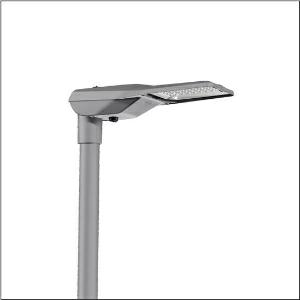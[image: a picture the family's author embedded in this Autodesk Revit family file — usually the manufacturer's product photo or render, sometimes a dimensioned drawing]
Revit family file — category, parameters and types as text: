
# Revit family: streetlight_sl_21_iq_mini___st1_0a_5xe2d31y08hb_7569
name_source: partatom
category: Lighting Fixtures
units: mm (PartAtom-declared; Revit-internal decimal feet)

## family parameters
Cut with Voids When Loaded = No
Host = Face
Light Source = No
Part Type = Normal
Room Calculation Point = No
Round Connector Dimension = Use Diameter
Shared = No

## types (1)
- --- (1 x LED, 9750 lm, 71 W, 3000K)
    Apparent Load = 71 VA
    CIE Flux Codes = 37 72 97 100 100
    Color Rendering = 70
    Color Temperature = 3000K
    Default Elevation = 1800 mm
    Description = Streetlight SL 21 iQ mini, mast luminaire, primary light control with lens, of PMMA, primary optical cover: cover, of toughened safety glass, transparent, light distribution: ST1.0a, light emission: direct distribution, primary light characteristic: asymmetric, installation type: post-top, side-entry, LED, High Power LED, rated luminous flux: 9.750lm, luminous efficacy: 137lm/W, light colour: 730, colour temperature: 3000K, control: presetting dimming logarithmic, Street-Remote, Auto-Match, Temp-Guard, Lumen-Switch, Night-Set, Smart-Wire, Light-Fading, Desk-Remote (wireless, voltage-free reading and setting of iQ features in the workshop via application-optimized NFC function/RFID function), optimised constant luminous flux control (CLO 2.0), mains connection: 220..240V, AC, 50/60Hz, start of lifetime: 71W, end of service life: 75W, reduction: 30W, luminaire housing, of diecast aluminium, powder-coated, Siteco® metallic grey (DB 702S), corrosivity category C5 mid according to DIN EN ISO 12944, please order mast flange separately, inclination adjustable: 0°, 5°, 10°, 15°, sealing non-destructively replaceable, multi-level sealing system, length: 628mm, width: 235mm, height: 110mm, mast flange for spigot size: 42mm (side-entry): 5XC10008XM4, 60/48mm (side-entry/post-top): 5XC10108XM2, 76/60mm (side-entry/post-top): 5XC10108XM1, Smart Interface below and above, protection rating (complete): IP66, insulation class (complete): insulation class II (safety insulation), certification: CE, ENEC, ENEC+, VDE, impact resistance: IK09, permissible operating ambient temperature for outdoor applications: -40..+50°C, standard-compliant lighting for roads and squares, packaging unit: 1 piece

Light Distribution: ST1.0a
    Height = 110 mm
    Lamp = 1 x LED
    Lamp Light Flux = 9750 lm
    Lamp Power = 71 W
    Lamp count = 1
    Length = 625 mm
    Luminous efficacy = 137 lm/W
    Manufacturer = Siteco
    ModVariant = No
    Model = 5XE2D31Y08HB
    Number of Poles = 1
    OnlyDefault = Yes
    Power Factor = 1
    Product Name = Streetlight SL 21 iQ mini | ST1.0a
    Product group = mast luminaire | pylon top
    ProductGroupID = 6100
    Protection Class = Protection class II
    Protection Degree = IP 66
    RLX_Detail_Level = 1
    RLX_Emergency_Light_Flux = 0 lm
    RLX_Emergency_Type = 0
    RLX_Emergency_Type_DB = No
    RlxData = <blob elided: 92997 chars, md5=56ee6b97>
    Socket = socket
    Standby Power = 0 W
    System Light Flux = 9750 lm
    System Power = 71 W
    Type Comments = factory setting: luminous flux: 100 % | dim-lin: 254 | 716 mA
    Type Image = l_1003514.jpg
    URL = http://relux.com
    VarID = @adj_063073
    Voltage = 0 V
    Weight = 0.00 kg
    Width = 234 mm

## geometry (parser evidence)
native form markers: Blend x4, Sweep x9
no freeform markers — native parametric forms only
